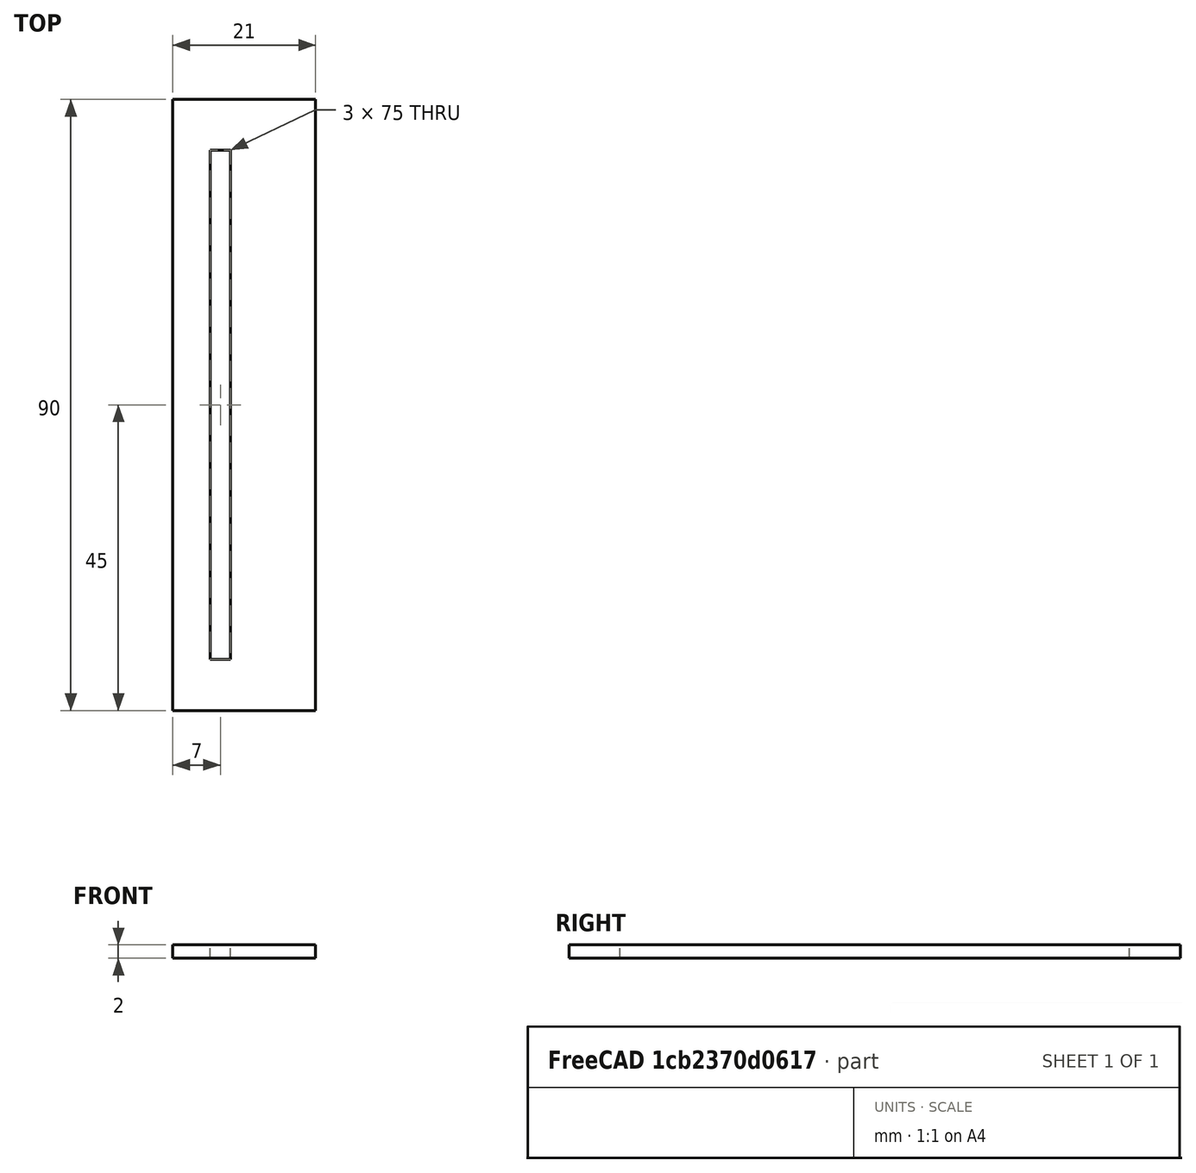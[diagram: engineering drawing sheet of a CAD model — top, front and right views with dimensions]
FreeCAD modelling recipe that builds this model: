
FCSTD DOCUMENT  (FreeCAD 0.20R29410 (Git))
Label: Silder
License: All rights reserved
LicenseURL: http://en.wikipedia.org/wiki/All_rights_reserved
objects: PartDesign::CoordinateSystem×4, App::DocumentObjectGroup×3, Part::FeaturePython×2, App::FeaturePython×1, Sketcher::SketchObject×1, PartDesign::Pad×1, PartDesign::Body×1, App::Part×1
note: 10 computed .brp shape members not serialized (recipe doc carries the construction recipe); baked Part::Feature solids carry a one-line shape summary decoded from their .brp
EXTERNAL_REF file=../../../../.cache/FreeCAD/Cache/FreeCAD_Doc_b944a62a-5acd-4748-8a46-371a6e0a0b2d_da39a3_75311 obj=LCS_Origin
EXTERNAL_REF file=../../../../.cache/FreeCAD/Cache/FreeCAD_Doc_b944a62a-5acd-4748-8a46-371a6e0a0b2d_da39a3_75311 obj=Assembly
EXTERNAL_REF file=Nut-Holder.FCStd obj=Assembly
EXTERNAL_REF file=../../../../.cache/FreeCAD/Cache/FreeCAD_Doc_43aa0dcd-2b8e-4044-a69a-189f3c988842_da39a3_75311 obj=LCS_Origin
EXTERNAL_REF file=../../../../.cache/FreeCAD/Cache/FreeCAD_Doc_43aa0dcd-2b8e-4044-a69a-189f3c988842_da39a3_75311 obj=Assembly

FEATURE [App::DocumentObjectGroup] Parts
FEATURE [PartDesign::CoordinateSystem] LCS_Origin
  AttacherType = Attacher::AttachEngine3D
  MapMode = 2
  Support = -> [X_Axis]
FEATURE [App::DocumentObjectGroup] Constraints
FEATURE [App::FeaturePython] Variables  # WARN: FeaturePython — macro-defined, semantics opaque (R4)
  Type = App::PropertyContainer
FEATURE [App::DocumentObjectGroup] Configurations
FEATURE [PartDesign::CoordinateSystem] LCS_0
  AttacherType = Attacher::AttachEngine3D
  MapMode = 2
  Support = -> [X_Axis001]
FEATURE [Sketcher::SketchObject] Sketch
  FullyConstrained = true
  MapMode = 5
  Support = -> [XY_Plane001]
  sketch-geometry (8):
    g0: LineSegment StartX=-10.5 StartY=45 StartZ=0 EndX=10.5 EndY=45 EndZ=0
    g1: LineSegment StartX=10.5 StartY=45 StartZ=0 EndX=10.5 EndY=-45 EndZ=0
    g2: LineSegment StartX=10.5 StartY=-45 StartZ=0 EndX=-10.5 EndY=-45 EndZ=0
    g3: LineSegment StartX=-10.5 StartY=-45 StartZ=0 EndX=-10.5 EndY=45 EndZ=0
    g4: LineSegment StartX=-5 StartY=37.5 StartZ=0 EndX=-2 EndY=37.5 EndZ=0
    g5: LineSegment StartX=-2 StartY=37.5 StartZ=0 EndX=-2 EndY=-37.5 EndZ=0
    g6: LineSegment StartX=-2 StartY=-37.5 StartZ=0 EndX=-5 EndY=-37.5 EndZ=0
    g7: LineSegment StartX=-5 StartY=-37.5 StartZ=0 EndX=-5 EndY=37.5 EndZ=0
  constraints (23):
    c: Coincident(g0,g1)
    c: Coincident(g1,g2)
    c: Coincident(g2,g3)
    c: Coincident(g3,g0)
    c: Horizontal(g0)
    c: Horizontal(g2)
    c: Vertical(g1)
    c: Vertical(g3)
    c: Symmetric(g0,g1,g-1)
    c: DistanceY(g1,g1) = 90
    c: DistanceX(g0,g0) = 21
    c: Coincident(g4,g5)
    c: Coincident(g5,g6)
    c: Coincident(g6,g7)
    c: Coincident(g7,g4)
    c: Horizontal(g4)
    c: Horizontal(g6)
    c: Vertical(g5)
    c: Vertical(g7)
    c: DistanceY(g7,g7) = 75
    c: DistanceX(g4,g4) = 3
    c: DistanceX(g2,g6) = 5.5
    c: DistanceY(g2,g6) = 7.5
FEATURE [PartDesign::Pad] Pad
  Direction = (0,0,1)
  Length = 2
  Length2 = 10
  Profile = -> Sketch
  ReferenceAxis = -> Sketch [N_Axis]
  Type = 0
FEATURE [PartDesign::Body] Body
  Group = -> [LCS_0,Sketch,Pad]
  Origin = -> Origin001
  Tip = -> Pad
FEATURE [PartDesign::CoordinateSystem] LCS_TL_Nut_Holder
  AttacherType = Attacher::AttachEngine3D
  AttachmentOffset = pos=(-3,3,0) rot=(0,0,1;0rad)
  MapMode = 6
  Placement = pos=(-7.5,42,2) rot=(0,0,1;3.14159rad)
  Support = -> [Pad]
FEATURE [PartDesign::CoordinateSystem] LCS_BR_Nut_Holder
  AttacherType = Attacher::AttachEngine3D
  AttachmentOffset = pos=(3,-3,0) rot=(0,0,1;0rad)
  MapMode = 6
  Placement = pos=(7.5,-42,2) rot=(0,0,1;3.14159rad)
  Support = -> [Pad]
FEATURE [Part::FeaturePython] Nut_Holder_TL  # link proxy (typed FeaturePython)
  AttachedBy = #LCS_Origin
  AttachedTo = Parent Assembly#LCS_TL_Nut_Holder
  LinkedObject = -> <external ../../../../.cache/FreeCAD/Cache/FreeCAD_Doc_b944a62a-5acd-4748-8a46-371a6e0a0b2d_da39a3_75311>#Assembly
  Placement = pos=(-7.5,42,2) rot=(0,0,1;3.14159rad)
  SolverId = Asm4EE
  SourceObject = -> <external Nut-Holder.FCStd>#Assembly
  Type = Asm4::VariantLink
  diameter = 8.6
  height = 9.2
  nut_width = 6
  pocket_height = 4.8
  expr: Placement = LCS_TL_Nut_Holder.Placement * AttachmentOffset * varTmpDoc_3#LCS_Origin.Placement ^ -1
FEATURE [Part::FeaturePython] Nut_Holder_BR  # link proxy (typed FeaturePython)
  AttachedBy = #LCS_Origin
  AttachedTo = Parent Assembly#LCS_BR_Nut_Holder
  LinkedObject = -> <external ../../../../.cache/FreeCAD/Cache/FreeCAD_Doc_43aa0dcd-2b8e-4044-a69a-189f3c988842_da39a3_75311>#Assembly
  Placement = pos=(7.5,-42,2) rot=(0,0,1;3.14159rad)
  SolverId = Asm4EE
  SourceObject = -> <external Nut-Holder.FCStd>#Assembly
  Type = Asm4::VariantLink
  diameter = 8.6
  height = 9.2
  nut_width = 6
  pocket_height = 4.8
  expr: Placement = LCS_BR_Nut_Holder.Placement * AttachmentOffset * varTmpDoc_4#LCS_Origin.Placement ^ -1
FEATURE [App::Part] Model
  AssemblyType = Part::Link
  Group = -> [LCS_Origin,Constraints,Variables,Configurations,Body,LCS_TL_Nut_Holder,LCS_BR_Nut_Holder,Nut_Holder_TL,Nut_Holder_BR]
  Origin = -> Origin
  Type = Assembly
